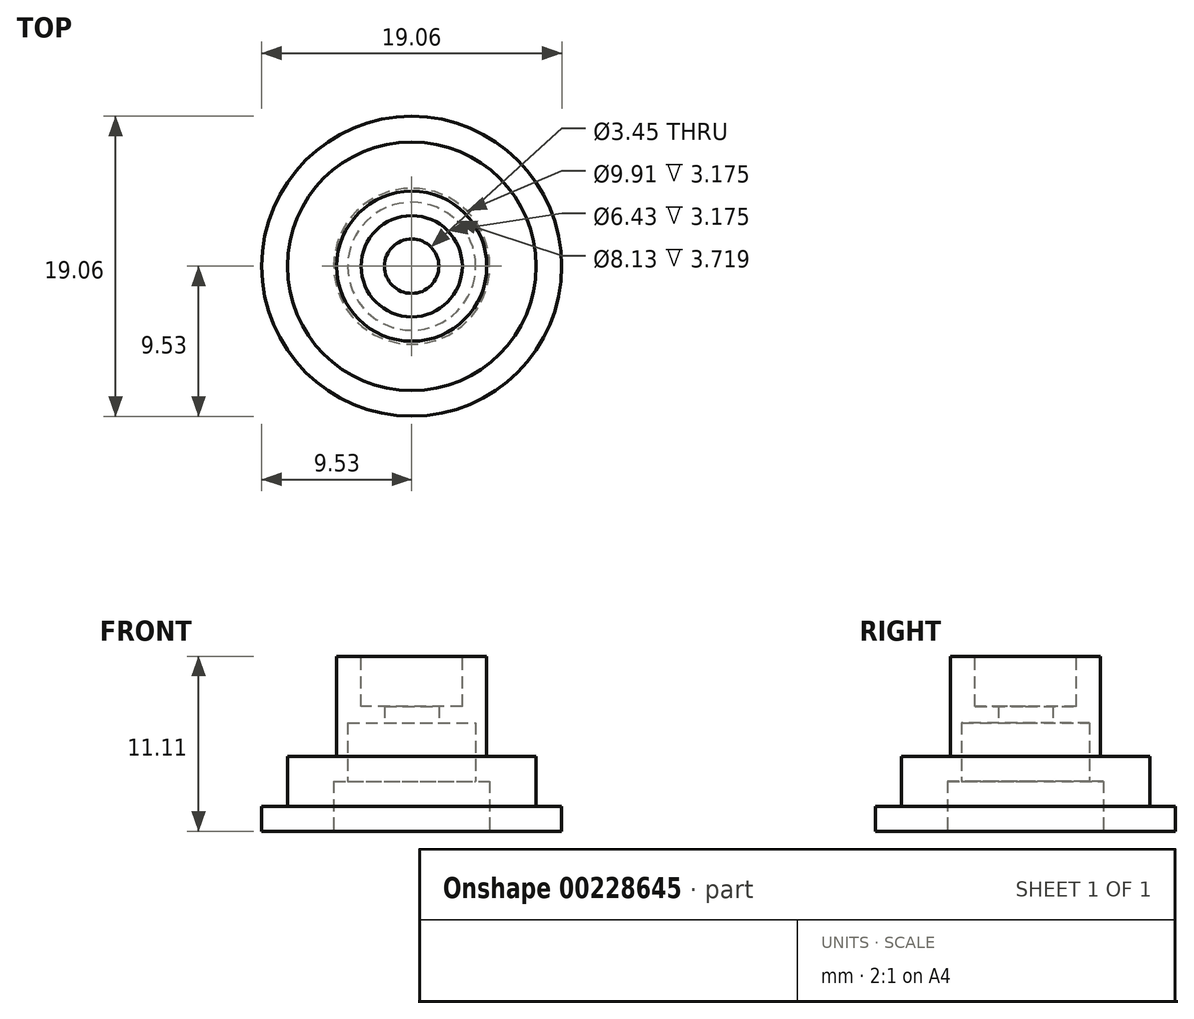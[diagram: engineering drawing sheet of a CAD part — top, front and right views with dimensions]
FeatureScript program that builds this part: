
annotation { "Feature Type Name" : "Feature", "Feature Type Description" : "" }
export const myFeature = defineFeature(function(context is Context, id is Id, definition is map)
    precondition{}
    {
        {
            var Q0;
            Q0=qCreatedBy(makeId("Top.planeOp"),FACE);
            var sketch = newSketch(context, id + "F0", { "sketchPlane" : qUnion([Q0])});
            skCircle(sketch, "E0", {"center": v(0, 0) * mm, "radius": 9.53 * mm});
            skSolve(sketch);
        }
        {
            var Q0;
            Q0 = qSketchRegion(id + "F0", true);
            extrude(context, id + "F1", {"entities" : qUnion([Q0]), "depth" : 1.59 * mm});
        }
        {
            var Q0;
            Q0=makeQuery(id+"F1.opExtrude","CAP_FACE",FACE,{"disambiguationData":[OSD([sQuery(id+"F0.wireOp",EDGE,"E0")])],"isStart":false});
            var sketch = newSketch(context, id + "F2", { "sketchPlane" : qUnion([Q0])});
            skCircle(sketch, "E1", {"center": v(0, 0) * mm, "radius": 7.9 * mm});
            skSolve(sketch);
        }
        {
            var Q0;
            Q0 = qSketchRegion(id + "F2", true);
            extrude(context, id + "F3", {"entities" : qUnion([Q0]), "operationType" : NewBodyOperationType.ADD, "depth" : 3.17 * mm});
        }
        {
            var Q0;
            Q0=makeQuery(id+"F1.opExtrude","CAP_FACE",FACE,{"disambiguationData":[OSD([sQuery(id+"F0.wireOp",EDGE,"E0")])],"isStart":true});
            var sketch = newSketch(context, id + "F4", { "sketchPlane" : qUnion([Q0])});
            skCircle(sketch, "E2", {"center": v(0, 0) * mm, "radius": 4.95 * mm});
            skSolve(sketch);
        }
        {
            var Q0;
            Q0 = qSketchRegion(id + "F4", true);
            extrude(context, id + "F5", {"entities" : qUnion([Q0]), "operationType" : NewBodyOperationType.REMOVE, "oppositeDirection" : true, "depth" : 3.17 * mm});
        }
        {
            var Q0;
            Q0=makeQuery(id+"F5.boolean.opBoolean","COPY",FACE,{"derivedFrom":makeQuery(id+"F5.opExtrude","CAP_FACE",FACE,{"disambiguationData":[OSD([sQuery(id+"F4.wireOp",EDGE,"E2")])],"isStart":false})});
            var sketch = newSketch(context, id + "F6", { "sketchPlane" : qUnion([Q0])});
            skCircle(sketch, "E3", {"center": v(0, 0) * mm, "radius": 1.73 * mm});
            skSolve(sketch);
        }
        {
            var Q0;
            Q0 = qSketchRegion(id + "F6", true);
            extrude(context, id + "F7", {"entities" : qUnion([Q0]), "operationType" : NewBodyOperationType.REMOVE, "endBound" : BoundingType.THROUGH_ALL, "oppositeDirection" : true, "depth" : 25.4 * mm});
        }
        {
            var Q0;
            Q0=makeQuery(id+"F3.opExtrude","CAP_FACE",FACE,{"disambiguationData":[OSD([sQuery(id+"F2.wireOp",EDGE,"E1")])],"isStart":false});
            var sketch = newSketch(context, id + "F8", { "sketchPlane" : qUnion([Q0])});
            skCircle(sketch, "E4", {"center": v(0, 0) * mm, "radius": 1.73 * mm});
            skCircle(sketch, "E5", {"center": v(0, 0) * mm, "radius": 4.76 * mm});
            skSolve(sketch);
        }
        {
            var Q0;
            Q0 = qSketchRegion(id + "F8", true);
            extrude(context, id + "F9", {"entities" : qUnion([Q0]), "operationType" : NewBodyOperationType.ADD, "depth" : 6.35 * mm});
        }
        {
            var Q0;
            Q0=makeQuery(id+"F9.opExtrude","CAP_FACE",FACE,{"disambiguationData":[OSD([sQuery(id+"F8.wireOp",EDGE,"E4"),sQuery(id+"F8.wireOp",EDGE,"E5")])],"isStart":false});
            var sketch = newSketch(context, id + "F10", { "sketchPlane" : qUnion([Q0])});
            skCircle(sketch, "E6", {"center": v(0, 0) * mm, "radius": 3.21 * mm});
            skSolve(sketch);
        }
        {
            var Q0;
            Q0 = qSketchRegion(id + "F10", true);
            extrude(context, id + "F11", {"entities" : qUnion([Q0]), "operationType" : NewBodyOperationType.REMOVE, "oppositeDirection" : true, "depth" : 3.17 * mm});
        }
        {
            var Q0;
            Q0=makeQuery(id+"F5.boolean.opBoolean","COPY",FACE,{"derivedFrom":makeQuery(id+"F5.opExtrude","CAP_FACE",FACE,{"disambiguationData":[OSD([sQuery(id+"F4.wireOp",EDGE,"E2")])],"isStart":false})});
            var sketch = newSketch(context, id + "F12", { "sketchPlane" : qUnion([Q0])});
            skCircle(sketch, "E7", {"center": v(0, 0) * mm, "radius": 4.06 * mm});
            skSolve(sketch);
        }
        {
            var Q0;
            Q0 = qSketchRegion(id + "F12", true);
            extrude(context, id + "F13", {"entities" : qUnion([Q0]), "operationType" : NewBodyOperationType.REMOVE, "oppositeDirection" : true, "depth" : 3.72 * mm});
        }
    });
